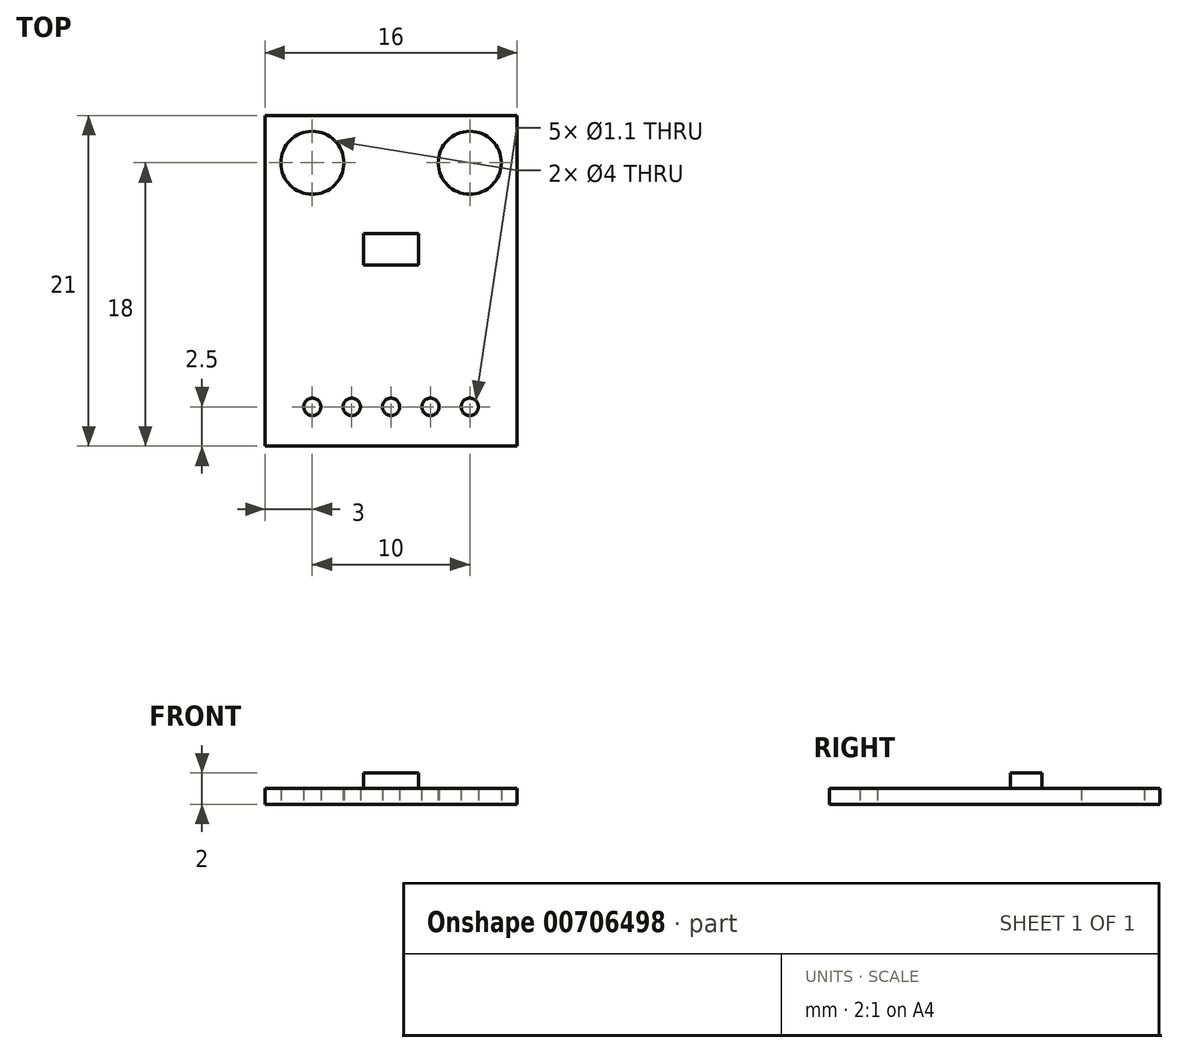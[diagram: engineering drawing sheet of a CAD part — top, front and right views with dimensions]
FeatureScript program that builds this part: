
annotation { "Feature Type Name" : "Feature", "Feature Type Description" : "" }
export const myFeature = defineFeature(function(context is Context, id is Id, definition is map)
    precondition{}
    {
        {
            var Q0;
            Q0=qCreatedBy(makeId("Top.planeOp"),FACE);
            var sketch = newSketch(context, id + "F0", { "sketchPlane" : qUnion([Q0])});
            skLineSegment(sketch, "E0.bottom", {"start": v(8, -10.5) * mm, "end": v(-8, -10.5) * mm});
            skLineSegment(sketch, "E0.top", {"start": v(8, 10.5) * mm, "end": v(-8, 10.5) * mm});
            skLineSegment(sketch, "E0.left", {"start": v(8, -10.5) * mm, "end": v(8, 10.5) * mm});
            skLineSegment(sketch, "E0.right", {"start": v(-8, -10.5) * mm, "end": v(-8, 10.5) * mm});
            skPoint(sketch, "E0.middle", {"position": v(0, 0) * mm});
            skPoint(sketch, "E1", {"position": v(-5, -8) * mm});
            skPoint(sketch, "E2.1.0.0", {"position": v(-2.5, -8) * mm});
            skPoint(sketch, "E2.2.0.0", {"position": v(0, -8) * mm});
            skPoint(sketch, "E2.3.0.0", {"position": v(2.5, -8) * mm});
            skPoint(sketch, "E2.4.0.0", {"position": v(5, -8) * mm});
            skLineSegment(sketch, "E2.direction1", {"start": v(-6, -8.5) * mm, "end": v(-3.5, -8.5) * mm, "construction": true});
            skPoint(sketch, "E3", {"position": v(-5, 7.5) * mm});
            skPoint(sketch, "E4.MirrorP", {"position": v(5, 7.5) * mm});
            skSolve(sketch);
        }
        {
            var Q0;
            Q0=makeQuery(id+"F0.imprint","IMPRINT",FACE,{"disambiguationData":[TD([[makeQuery(id+"F0.imprint","IMPRINT",EDGE,{"derivedFrom":sQuery(id+"F0.wireOp",EDGE,"E0.bottom")}),-1.0]])]});
            extrude(context, id + "F1", {"entities" : qUnion([Q0]), "depth" : 1 * mm, "offsetDistance" : 25 * mm});
        }
        {
            var Q0;
            Q0=sQuery(id+"F0.wireOp",VERTEX,"E1");
            var Q1;
            Q1=sQuery(id+"F0.wireOp",VERTEX,"E2.1.0.0");
            var Q2;
            Q2=sQuery(id+"F0.wireOp",VERTEX,"E2.2.0.0");
            var Q3;
            Q3=sQuery(id+"F0.wireOp",VERTEX,"E2.3.0.0");
            var Q4;
            Q4=sQuery(id+"F0.wireOp",VERTEX,"E2.4.0.0");
            var Q5;
            Q5=makeQuery(id+"F1.opExtrude","SWEPT_BODY",BODY,{"disambiguationData":[OSD([sQuery(id+"F0.wireOp",EDGE,"E0.bottom"),sQuery(id+"F0.wireOp",EDGE,"E0.top"),sQuery(id+"F0.wireOp",EDGE,"E0.left"),sQuery(id+"F0.wireOp",EDGE,"E0.right")])]});
            hole(context, id + "F2", {"style" : HoleStyle.SIMPLE, "endStyle" : HoleEndStyle.THROUGH, "oppositeDirection" : true, "holeDiameter" : 1.1 * mm, "majorDiameter" : 5 * mm, "isTappedThrough" : true, "tappedDepth" : 6 * mm, "tapClearance" : 3, "locations" : qUnion([Q0, Q1, Q2, Q3, Q4]), "scope" : qUnion([Q5])});
        }
        {
            var Q0;
            Q0=sQuery(id+"F0.wireOp",VERTEX,"E3");
            var Q1;
            Q1=sQuery(id+"F0.wireOp",VERTEX,"E4.MirrorP");
            var Q2;
            Q2=makeQuery(id+"F1.opExtrude","SWEPT_BODY",BODY,{"disambiguationData":[OSD([sQuery(id+"F0.wireOp",EDGE,"E0.bottom"),sQuery(id+"F0.wireOp",EDGE,"E0.top"),sQuery(id+"F0.wireOp",EDGE,"E0.left"),sQuery(id+"F0.wireOp",EDGE,"E0.right")])]});
            hole(context, id + "F3", {"style" : HoleStyle.SIMPLE, "endStyle" : HoleEndStyle.THROUGH, "oppositeDirection" : true, "holeDiameter" : 4 * mm, "majorDiameter" : 5 * mm, "isTappedThrough" : true, "tappedDepth" : 6 * mm, "tapClearance" : 3, "locations" : qUnion([Q0, Q1]), "scope" : qUnion([Q2])});
        }
        {
            var Q0;
            Q0=makeQuery(id+"F1.opExtrude","CAP_FACE",FACE,{"disambiguationData":[OSD([sQuery(id+"F0.wireOp",EDGE,"E0.bottom"),sQuery(id+"F0.wireOp",EDGE,"E0.top"),sQuery(id+"F0.wireOp",EDGE,"E0.left"),sQuery(id+"F0.wireOp",EDGE,"E0.right")])],"isStart":false});
            var sketch = newSketch(context, id + "F4", { "sketchPlane" : qUnion([Q0])});
            skLineSegment(sketch, "E5.bottom", {"start": v(1.75, 1) * mm, "end": v(-1.75, 1) * mm});
            skLineSegment(sketch, "E5.top", {"start": v(1.75, 3) * mm, "end": v(-1.75, 3) * mm});
            skLineSegment(sketch, "E5.left", {"start": v(1.75, 1) * mm, "end": v(1.75, 3) * mm});
            skLineSegment(sketch, "E5.right", {"start": v(-1.75, 1) * mm, "end": v(-1.75, 3) * mm});
            skPoint(sketch, "E5.middle", {"position": v(0, 2) * mm});
            skSolve(sketch);
        }
        {
            var Q0;
            Q0=makeQuery(id+"F4.imprint","IMPRINT",FACE,{"disambiguationData":[TD([[makeQuery(id+"F4.imprint","IMPRINT",EDGE,{"derivedFrom":sQuery(id+"F4.wireOp",EDGE,"E5.bottom")}),-1.0]])]});
            extrude(context, id + "F5", {"entities" : qUnion([Q0]), "depth" : 1 * mm, "offsetDistance" : 25 * mm});
        }
    });
